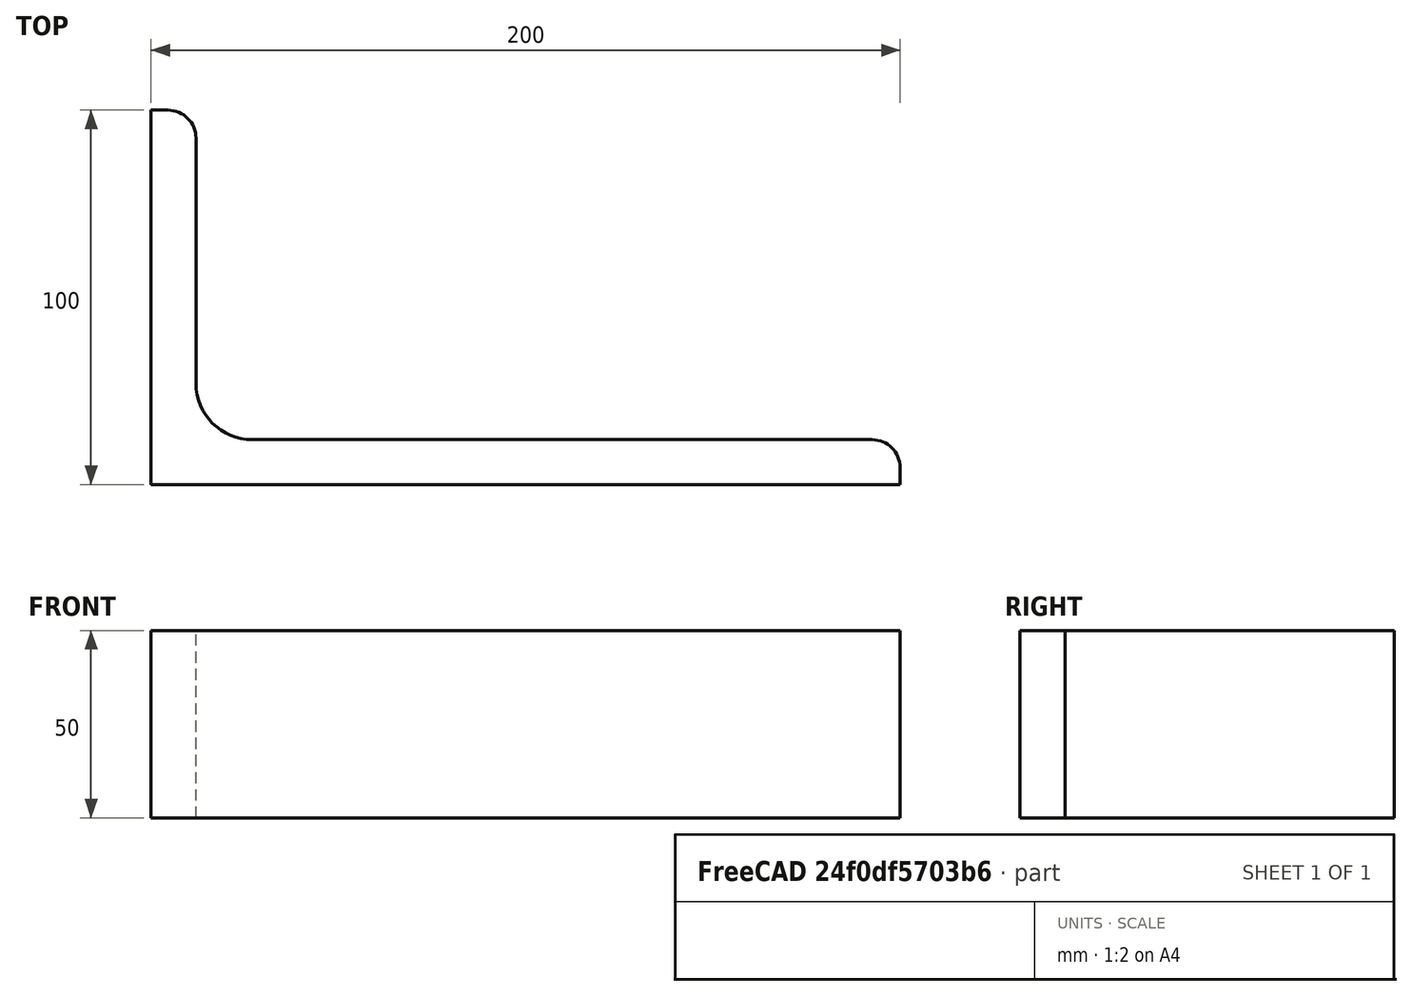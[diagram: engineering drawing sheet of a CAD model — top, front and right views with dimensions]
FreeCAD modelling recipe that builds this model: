
FCSTD DOCUMENT  (FreeCAD 0.15R4671 (Git))
Label: Angle Bar 200x100x12 EN10056 S235JR
License: All rights reserved
LicenseURL: http://en.wikipedia.org/wiki/All_rights_reserved
objects: Sketcher::SketchObject×1, Part::Extrusion×1
note: 2 computed .brp shape members not serialized (recipe doc carries the construction recipe); baked Part::Feature solids carry a one-line shape summary decoded from their .brp

FEATURE [Sketcher::SketchObject] Sketch
  sketch-geometry (9):
    g0: LineSegment StartX=0 StartY=0 StartZ=0 EndX=200 EndY=0 EndZ=0
    g1: LineSegment StartX=200 StartY=0 StartZ=0 EndX=200 EndY=4.5 EndZ=0
    g2: LineSegment StartX=192.5 StartY=12 StartZ=0 EndX=27 EndY=12 EndZ=0
    g3: LineSegment StartX=0 StartY=0 StartZ=0 EndX=0 EndY=100 EndZ=0
    g4: LineSegment StartX=0 StartY=100 StartZ=0 EndX=4.5 EndY=100 EndZ=0
    g5: LineSegment StartX=12 StartY=92.5 StartZ=0 EndX=12 EndY=27 EndZ=0
    g6: ArcOfCircle CenterX=27 CenterY=27 CenterZ=0 NormalX=0 NormalY=0 NormalZ=1 Radius=15 StartAngle=3.14159 EndAngle=4.71239
    g7: ArcOfCircle CenterX=4.5 CenterY=92.5 CenterZ=0 NormalX=0 NormalY=0 NormalZ=1 Radius=7.5 StartAngle=0 EndAngle=1.5708
    g8: ArcOfCircle CenterX=192.5 CenterY=4.5 CenterZ=0 NormalX=0 NormalY=0 NormalZ=1 Radius=7.5 StartAngle=0 EndAngle=1.5708
  constraints (23):
    c: Coincident(g0,g-1)
    c: Horizontal(g0)
    c: Coincident(g1,g0)
    c: Vertical(g1)
    c: Horizontal(g2)
    c: Coincident(g3,g-1)
    c: Vertical(g3)
    c: Coincident(g4,g3)
    c: Horizontal(g4)
    c: Vertical(g5)
    c: Tangent(g5,g6) = -1.5708
    c: Tangent(g2,g6) = 1.5708
    c: Tangent(g4,g7) = 1.5708
    c: Tangent(g5,g7) = 1.5708
    c: Tangent(g2,g8) = -1.5708
    c: Tangent(g1,g8) = -1.5708
    c: DistanceX(g0) = 200
    c: DistanceY(g3) = 100
    c: DistanceY(g0,g2) = 12
    c: DistanceX(g3,g5) = 12
    c: Radius(g6) = 15
    c: Radius(g8) = 7.5
    c: Radius(g7) = 7.5
FEATURE [Part::Extrusion] Extrude  label="Angle Bar 200x100x12 EN10056 S235JR"
  Base = -> Sketch
  Dir = (0,0,50)
  Solid = true
